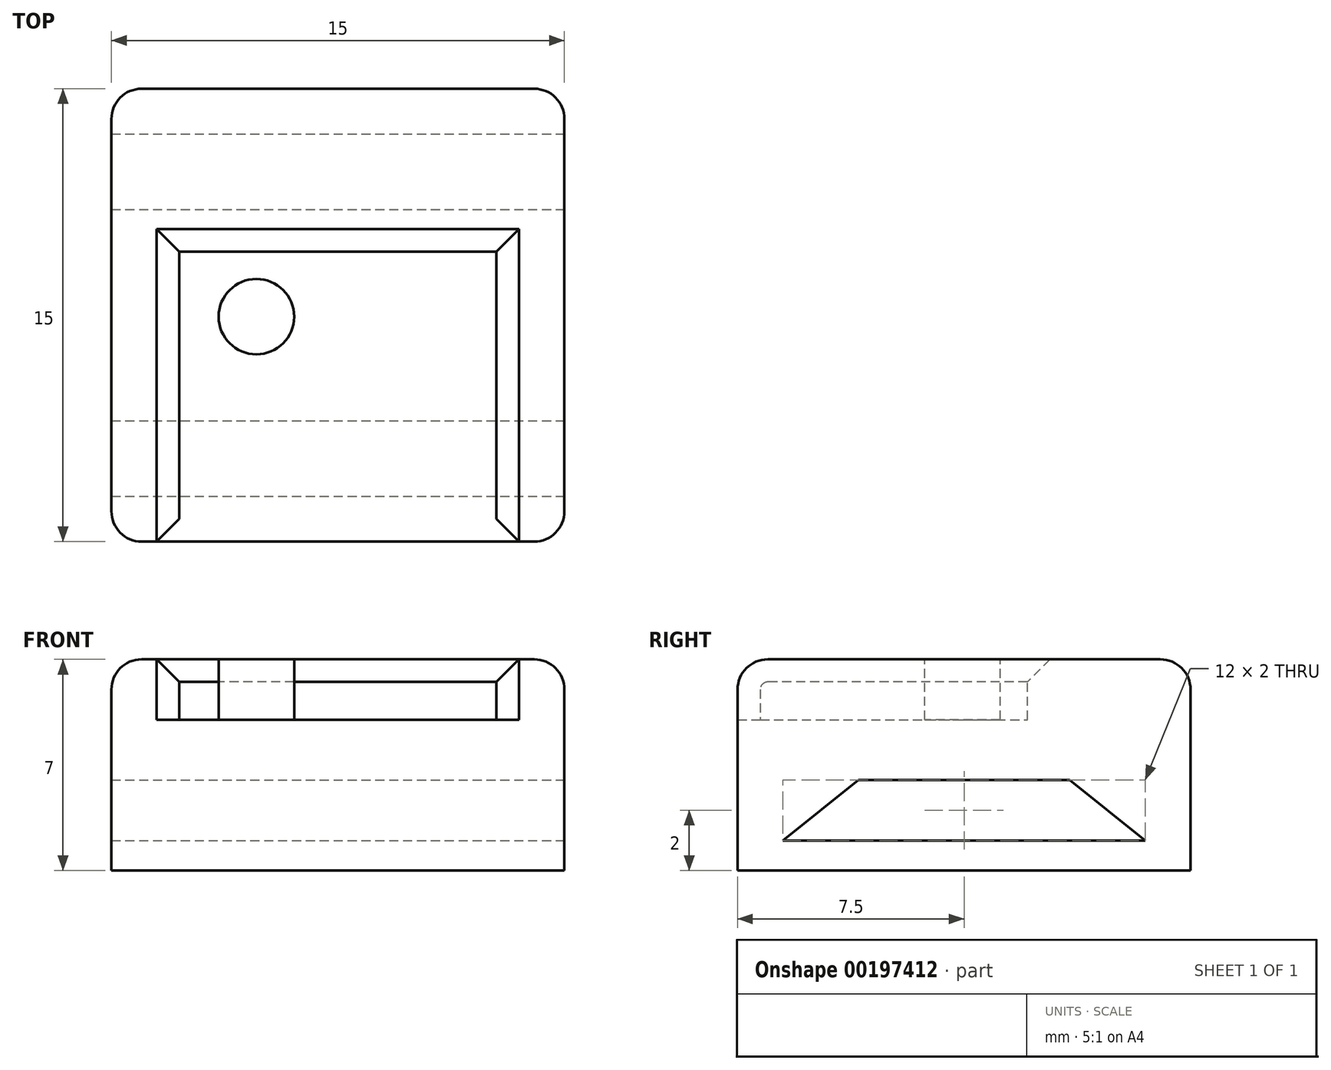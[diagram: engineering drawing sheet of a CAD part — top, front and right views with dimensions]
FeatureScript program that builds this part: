
annotation { "Feature Type Name" : "Feature", "Feature Type Description" : "" }
export const myFeature = defineFeature(function(context is Context, id is Id, definition is map)
    precondition{}
    {
        {
            var Q0;
            Q0=qCreatedBy(makeId("Top.planeOp"),FACE);
            var sketch = newSketch(context, id + "F0", { "sketchPlane" : qUnion([Q0])});
            skLineSegment(sketch, "E0.bottom", {"start": v(7.5, 7.5) * mm, "end": v(-7.5, 7.5) * mm});
            skLineSegment(sketch, "E0.top", {"start": v(7.5, -7.5) * mm, "end": v(-7.5, -7.5) * mm});
            skLineSegment(sketch, "E0.left", {"start": v(7.5, 7.5) * mm, "end": v(7.5, -7.5) * mm});
            skLineSegment(sketch, "E0.right", {"start": v(-7.5, 7.5) * mm, "end": v(-7.5, -7.5) * mm});
            skPoint(sketch, "E0.middle", {"position": v(0, 0) * mm});
            skSolve(sketch);
        }
        {
            var Q0;
            Q0 = qSketchRegion(id + "F0", true);
            extrude(context, id + "F1", {"entities" : qUnion([Q0]), "depth" : 4 * mm});
        }
        {
            var Q0;
            Q0=makeQuery(id+"F1.opExtrude","CAP_FACE",FACE,{"disambiguationData":[OSD([sQuery(id+"F0.wireOp",EDGE,"E0.bottom"),sQuery(id+"F0.wireOp",EDGE,"E0.top"),sQuery(id+"F0.wireOp",EDGE,"E0.left"),sQuery(id+"F0.wireOp",EDGE,"E0.right")])],"isStart":false});
            var sketch = newSketch(context, id + "F2", { "sketchPlane" : qUnion([Q0])});
            skLineSegment(sketch, "E1.bottom", {"start": v(-5.25, -7.5) * mm, "end": v(5.25, -7.5) * mm});
            skLineSegment(sketch, "E1.top", {"start": v(-5.25, 2.1) * mm, "end": v(5.25, 2.1) * mm});
            skLineSegment(sketch, "E1.left", {"start": v(-5.25, -7.5) * mm, "end": v(-5.25, 2.1) * mm});
            skLineSegment(sketch, "E1.right", {"start": v(5.25, -7.5) * mm, "end": v(5.25, 2.1) * mm});
            skCircle(sketch, "E2", {"center": v(-2.7, -0.05) * mm, "radius": 1.25 * mm});
            skSolve(sketch);
        }
        {
            var Q0;
            Q0=makeQuery(id+"F2.imprint","IMPRINT",FACE,{"disambiguationData":[TD([[makeQuery(id+"F2.imprint","IMPRINT",EDGE,{"derivedFrom":sQuery(id+"F2.wireOp",EDGE,"E1.bottom")}),-1.0]])]});
            extrude(context, id + "F3", {"entities" : qUnion([Q0]), "operationType" : NewBodyOperationType.REMOVE, "oppositeDirection" : true, "depth" : 2 * mm});
        }
        {
            var Q0;
            Q0=makeQuery(id+"F1.opExtrude","CAP_FACE",FACE,{"disambiguationData":[OSD([sQuery(id+"F0.wireOp",EDGE,"E0.bottom"),sQuery(id+"F0.wireOp",EDGE,"E0.top"),sQuery(id+"F0.wireOp",EDGE,"E0.left"),sQuery(id+"F0.wireOp",EDGE,"E0.right")])],"isStart":true});
            var sketch = newSketch(context, id + "F4", { "sketchPlane" : qUnion([Q0])});
            skLineSegment(sketch, "E3.bottom", {"start": v(7.5, 7.5) * mm, "end": v(-7.5, 7.5) * mm});
            skLineSegment(sketch, "E3.top", {"start": v(7.5, -7.5) * mm, "end": v(-7.5, -7.5) * mm});
            skLineSegment(sketch, "E3.left", {"start": v(7.5, 7.5) * mm, "end": v(7.5, -7.5) * mm});
            skLineSegment(sketch, "E3.right", {"start": v(-7.5, 7.5) * mm, "end": v(-7.5, -7.5) * mm});
            skPoint(sketch, "E3.middle", {"position": v(0, 0) * mm});
            skSolve(sketch);
        }
        {
            var Q0;
            Q0 = qSketchRegion(id + "F4", true);
            extrude(context, id + "F5", {"entities" : qUnion([Q0]), "operationType" : NewBodyOperationType.ADD, "depth" : 3 * mm});
        }
        {
            var Q0;
            Q0=makeQuery(id+"F5.boolean.opBoolean","MERGE",FACE,{"derivedFrom":[makeQuery(id+"F1.opExtrude","SWEPT_FACE",FACE,{"disambiguationData":[OSD([sQuery(id+"F0.wireOp",EDGE,"E0.left")])]}),makeQuery(id+"F5.opExtrude","SWEPT_FACE",FACE,{"disambiguationData":[OSD([sQuery(id+"F4.wireOp",EDGE,"E3.left")])]})]});
            var sketch = newSketch(context, id + "F6", { "sketchPlane" : qUnion([Q0])});
            skLineSegment(sketch, "E4", {"start": v(-6, -2) * mm, "end": v(6, -2) * mm});
            skLineSegment(sketch, "E5", {"start": v(6, -2) * mm, "end": v(3.5, 0) * mm});
            skLineSegment(sketch, "E6", {"start": v(3.5, 0) * mm, "end": v(-3.5, 0) * mm});
            skLineSegment(sketch, "E7", {"start": v(-3.5, 0) * mm, "end": v(-6, -2) * mm});
            skSolve(sketch);
        }
        {
            var Q0;
            Q0 = qSketchRegion(id + "F6", true);
            var Q1;
            Q1=makeQuery(id+"F5.boolean.opBoolean","MERGE",FACE,{"derivedFrom":[makeQuery(id+"F1.opExtrude","SWEPT_FACE",FACE,{"disambiguationData":[OSD([sQuery(id+"F0.wireOp",EDGE,"E0.right")])]}),makeQuery(id+"F5.opExtrude","SWEPT_FACE",FACE,{"disambiguationData":[OSD([sQuery(id+"F4.wireOp",EDGE,"E3.right")])]})]});
            extrude(context, id + "F7", {"entities" : qUnion([Q0]), "operationType" : NewBodyOperationType.REMOVE, "endBound" : BoundingType.UP_TO_SURFACE, "oppositeDirection" : true, "endBoundEntityFace" : qUnion([Q1]), "depth" : 25 * mm});
        }
        {
            var Q0;
            Q0=makeQuery(id+"F1.opExtrude","CAP_EDGE",EDGE,{"disambiguationData":[OSD([sQuery(id+"F0.wireOp",EDGE,"E0.bottom")])],"isStart":false});
            var Q1;
            Q1=makeQuery(id+"F1.opExtrude","CAP_EDGE",EDGE,{"disambiguationData":[OSD([sQuery(id+"F0.wireOp",EDGE,"E0.right")])],"isStart":false});
            var Q2;
            Q2=makeQuery(id+"F1.opExtrude","CAP_EDGE",EDGE,{"disambiguationData":[OSD([sQuery(id+"F0.wireOp",EDGE,"E0.left")])],"isStart":false});
            var Q3;
            {var subQ0=sQuery(id+"F0.wireOp",EDGE,"E0.left");var subQ1=sQuery(id+"F0.wireOp",EDGE,"E0.top");Q3=makeQuery(id+"F3.boolean.opBoolean","SPLIT",EDGE,{"disambiguationData":[TD([makeQuery(id+"F1.opExtrude","SWEPT_FACE",FACE,{"disambiguationData":[OSD([subQ0])]})])],"derivedFrom":makeQuery(id+"F1.opExtrude","CAP_EDGE",EDGE,{"disambiguationData":[OSD([subQ1])],"isStart":false})});}
            var Q4;
            {var subQ0=sQuery(id+"F0.wireOp",EDGE,"E0.right");var subQ1=sQuery(id+"F0.wireOp",EDGE,"E0.top");Q4=makeQuery(id+"F3.boolean.opBoolean","SPLIT",EDGE,{"disambiguationData":[TD([makeQuery(id+"F1.opExtrude","SWEPT_FACE",FACE,{"disambiguationData":[OSD([subQ0])]})])],"derivedFrom":makeQuery(id+"F1.opExtrude","CAP_EDGE",EDGE,{"disambiguationData":[OSD([subQ1])],"isStart":false})});}
            var Q5;
            Q5=makeQuery(id+"F5.boolean.opBoolean","MERGE",EDGE,{"derivedFrom":[makeQuery(id+"F1.opExtrude","SWEPT_EDGE",EDGE,{"disambiguationData":[OSD([sQuery(id+"F0.wireOp",EDGE,"E0.bottom"),sQuery(id+"F0.wireOp",EDGE,"E0.right")])]}),makeQuery(id+"F5.opExtrude","SWEPT_EDGE",EDGE,{"disambiguationData":[OSD([sQuery(id+"F4.wireOp",EDGE,"E3.top"),sQuery(id+"F4.wireOp",EDGE,"E3.right")])]})]});
            var Q6;
            Q6=makeQuery(id+"F5.boolean.opBoolean","MERGE",EDGE,{"derivedFrom":[makeQuery(id+"F1.opExtrude","SWEPT_EDGE",EDGE,{"disambiguationData":[OSD([sQuery(id+"F0.wireOp",EDGE,"E0.top"),sQuery(id+"F0.wireOp",EDGE,"E0.right")])]}),makeQuery(id+"F5.opExtrude","SWEPT_EDGE",EDGE,{"disambiguationData":[OSD([sQuery(id+"F4.wireOp",EDGE,"E3.bottom"),sQuery(id+"F4.wireOp",EDGE,"E3.right")])]})]});
            var Q7;
            Q7=makeQuery(id+"F5.boolean.opBoolean","MERGE",EDGE,{"derivedFrom":[makeQuery(id+"F1.opExtrude","SWEPT_EDGE",EDGE,{"disambiguationData":[OSD([sQuery(id+"F0.wireOp",EDGE,"E0.top"),sQuery(id+"F0.wireOp",EDGE,"E0.left")])]}),makeQuery(id+"F5.opExtrude","SWEPT_EDGE",EDGE,{"disambiguationData":[OSD([sQuery(id+"F4.wireOp",EDGE,"E3.bottom"),sQuery(id+"F4.wireOp",EDGE,"E3.left")])]})]});
            var Q8;
            Q8=makeQuery(id+"F5.boolean.opBoolean","MERGE",EDGE,{"derivedFrom":[makeQuery(id+"F1.opExtrude","SWEPT_EDGE",EDGE,{"disambiguationData":[OSD([sQuery(id+"F0.wireOp",EDGE,"E0.bottom"),sQuery(id+"F0.wireOp",EDGE,"E0.left")])]}),makeQuery(id+"F5.opExtrude","SWEPT_EDGE",EDGE,{"disambiguationData":[OSD([sQuery(id+"F4.wireOp",EDGE,"E3.top"),sQuery(id+"F4.wireOp",EDGE,"E3.left")])]})]});
            fillet(context, id + "F8", {"entities" : qUnion([Q0, Q1, Q2, Q3, Q4, Q5, Q6, Q7, Q8]), "radius" : 1 * mm, "tangentPropagation" : true, "allowEdgeOverflow" : false});
        }
        {
            var Q0;
            Q0=makeQuery(id+"F3.boolean.opBoolean","COPY",EDGE,{"derivedFrom":makeQuery(id+"F3.opExtrude","CAP_EDGE",EDGE,{"disambiguationData":[OSD([sQuery(id+"F2.wireOp",EDGE,"E1.right")])],"isStart":true})});
            var Q1;
            Q1=makeQuery(id+"F3.boolean.opBoolean","COPY",EDGE,{"derivedFrom":makeQuery(id+"F3.opExtrude","CAP_EDGE",EDGE,{"disambiguationData":[OSD([sQuery(id+"F2.wireOp",EDGE,"E1.top")])],"isStart":true})});
            var Q2;
            Q2=makeQuery(id+"F3.boolean.opBoolean","COPY",EDGE,{"derivedFrom":makeQuery(id+"F3.opExtrude","CAP_EDGE",EDGE,{"disambiguationData":[OSD([sQuery(id+"F2.wireOp",EDGE,"E1.left")])],"isStart":true})});
            chamfer(context, id + "F9", {"entities" : qUnion([Q0, Q1, Q2]), "width" : .75 * mm, "tangentPropagation" : true});
        }
    });
